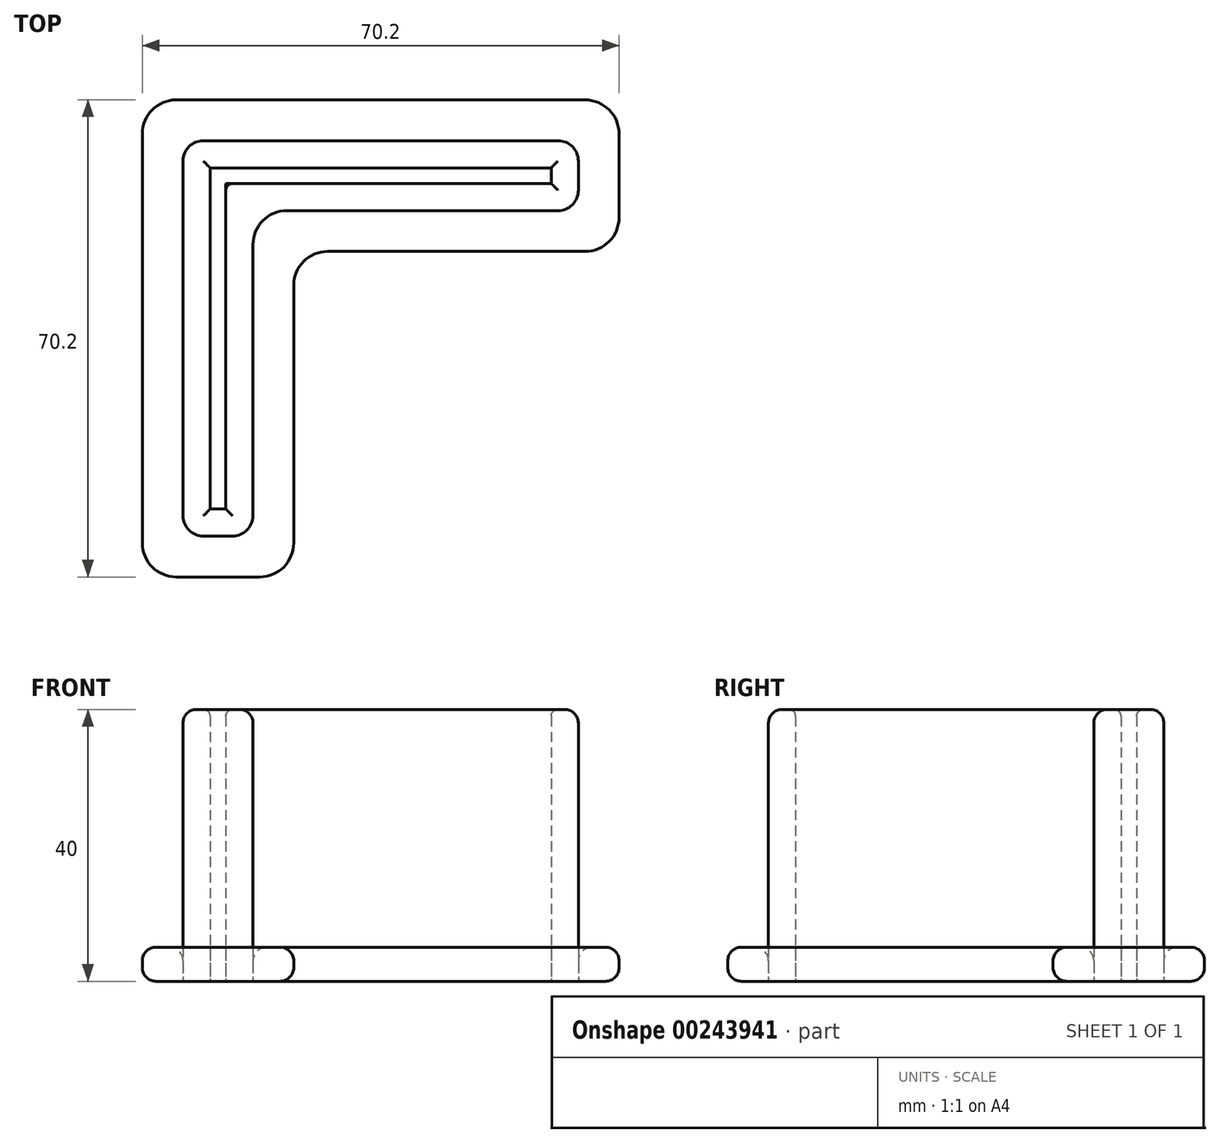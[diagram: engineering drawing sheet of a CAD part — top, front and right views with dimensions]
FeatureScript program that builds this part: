
annotation { "Feature Type Name" : "Feature", "Feature Type Description" : "" }
export const myFeature = defineFeature(function(context is Context, id is Id, definition is map)
    precondition{}
    {
        {
            var Q0;
            Q0=qCreatedBy(makeId("Top.planeOp"),FACE);
            var sketch = newSketch(context, id + "F0", { "sketchPlane" : qUnion([Q0])});
            skLineSegment(sketch, "E0", {"start": v(0, 0) * mm, "end": v(50.2, 0) * mm});
            skLineSegment(sketch, "E1", {"start": v(50.2, 0) * mm, "end": v(50.2, -2.3) * mm});
            skLineSegment(sketch, "E2", {"start": v(50.2, -2.3) * mm, "end": v(2.3, -2.3) * mm});
            skLineSegment(sketch, "E3", {"start": v(0, 0) * mm, "end": v(0, -50.2) * mm});
            skLineSegment(sketch, "E4", {"start": v(0, -50.2) * mm, "end": v(2.3, -50.2) * mm});
            skLineSegment(sketch, "E5", {"start": v(2.3, -50.2) * mm, "end": v(2.3, -2.3) * mm});
            skLineSegment(sketch, "E6.0", {"start": v(-5, 10) * mm, "end": v(55.2, 10) * mm});
            skLineSegment(sketch, "E7.0", {"start": v(60.2, 5) * mm, "end": v(60.2, -7.3) * mm});
            skLineSegment(sketch, "E8.0", {"start": v(55.2, -12.3) * mm, "end": v(17.3, -12.3) * mm});
            skLineSegment(sketch, "E9.0", {"start": v(12.3, -55.2) * mm, "end": v(12.3, -17.3) * mm});
            skLineSegment(sketch, "E10.0", {"start": v(-5, -60.2) * mm, "end": v(7.3, -60.2) * mm});
            skLineSegment(sketch, "E11.0", {"start": v(-10, 5) * mm, "end": v(-10, -55.2) * mm});
            skPoint(sketch, "E12.visualSharp", {"position": v(-10, 10) * mm});
            skArc(sketch, "E12.filletArc", {"start": v(-5, 10) * mm, "mid": v(-8.54, 8.54) * mm, "end": v(-10, 5) * mm});
            skPoint(sketch, "E13.visualSharp", {"position": v(60.2, 10) * mm});
            skArc(sketch, "E13.filletArc", {"start": v(60.2, 5) * mm, "mid": v(58.74, 8.54) * mm, "end": v(55.2, 10) * mm});
            skPoint(sketch, "E14.visualSharp", {"position": v(60.2, -12.3) * mm});
            skArc(sketch, "E14.filletArc", {"start": v(55.2, -12.3) * mm, "mid": v(58.74, -10.84) * mm, "end": v(60.2, -7.3) * mm});
            skPoint(sketch, "E15.visualSharp", {"position": v(12.3, -12.3) * mm});
            skArc(sketch, "E15.filletArc", {"start": v(17.3, -12.3) * mm, "mid": v(13.76, -13.76) * mm, "end": v(12.3, -17.3) * mm});
            skPoint(sketch, "E16.visualSharp", {"position": v(12.3, -60.2) * mm});
            skArc(sketch, "E16.filletArc", {"start": v(7.3, -60.2) * mm, "mid": v(10.84, -58.74) * mm, "end": v(12.3, -55.2) * mm});
            skPoint(sketch, "E17.visualSharp", {"position": v(-10, -60.2) * mm});
            skArc(sketch, "E17.filletArc", {"start": v(-10, -55.2) * mm, "mid": v(-8.54, -58.74) * mm, "end": v(-5, -60.2) * mm});
            skLineSegment(sketch, "E18.0", {"start": v(54.2, 1) * mm, "end": v(54.2, -3.3) * mm});
            skLineSegment(sketch, "E19.0", {"start": v(-1, 4) * mm, "end": v(51.2, 4) * mm});
            skLineSegment(sketch, "E20.0", {"start": v(51.2, -6.3) * mm, "end": v(11.3, -6.3) * mm});
            skLineSegment(sketch, "E21.0", {"start": v(6.3, -51.2) * mm, "end": v(6.3, -11.3) * mm});
            skLineSegment(sketch, "E22.0", {"start": v(-1, -54.2) * mm, "end": v(3.3, -54.2) * mm});
            skLineSegment(sketch, "E23.0", {"start": v(-4, 1) * mm, "end": v(-4, -51.2) * mm});
            skPoint(sketch, "E24.visualSharp", {"position": v(6.3, -6.3) * mm});
            skArc(sketch, "E24.filletArc", {"start": v(11.3, -6.3) * mm, "mid": v(7.76, -7.76) * mm, "end": v(6.3, -11.3) * mm});
            skPoint(sketch, "E25.visualSharp", {"position": v(-4, 4) * mm});
            skArc(sketch, "E25.filletArc", {"start": v(-1, 4) * mm, "mid": v(-3.12, 3.12) * mm, "end": v(-4, 1) * mm});
            skPoint(sketch, "E26.visualSharp", {"position": v(54.2, 4) * mm});
            skArc(sketch, "E26.filletArc", {"start": v(54.2, 1) * mm, "mid": v(53.32, 3.12) * mm, "end": v(51.2, 4) * mm});
            skPoint(sketch, "E27.visualSharp", {"position": v(54.2, -6.3) * mm});
            skArc(sketch, "E27.filletArc", {"start": v(51.2, -6.3) * mm, "mid": v(53.32, -5.42) * mm, "end": v(54.2, -3.3) * mm});
            skPoint(sketch, "E28.visualSharp", {"position": v(6.3, -54.2) * mm});
            skArc(sketch, "E28.filletArc", {"start": v(3.3, -54.2) * mm, "mid": v(5.42, -53.32) * mm, "end": v(6.3, -51.2) * mm});
            skPoint(sketch, "E29.visualSharp", {"position": v(-4, -54.2) * mm});
            skArc(sketch, "E29.filletArc", {"start": v(-4, -51.2) * mm, "mid": v(-3.12, -53.32) * mm, "end": v(-1, -54.2) * mm});
            skSolve(sketch);
        }
        {
            var Q0;
            Q0=makeQuery(id+"F0.imprint","IMPRINT",FACE,{"disambiguationData":[TD([[makeQuery(id+"F0.imprint","IMPRINT",EDGE,{"derivedFrom":sQuery(id+"F0.wireOp",EDGE,"E0")}),-1.0]])]});
            var Q1;
            Q1=makeQuery(id+"F0.imprint","IMPRINT",FACE,{"disambiguationData":[TD([[makeQuery(id+"F0.imprint","IMPRINT",EDGE,{"derivedFrom":sQuery(id+"F0.wireOp",EDGE,"E6.0")}),-1.0]])]});
            extrude(context, id + "F1", {"entities" : qUnion([Q0, Q1]), "depth" : 5 * mm});
        }
        {
            var Q0;
            Q0=makeQuery(id+"F0.imprint","IMPRINT",FACE,{"disambiguationData":[TD([[makeQuery(id+"F0.imprint","IMPRINT",EDGE,{"derivedFrom":sQuery(id+"F0.wireOp",EDGE,"E0")}),1.0]])]});
            extrude(context, id + "F2", {"entities" : qUnion([Q0]), "depth" : 40 * mm});
        }
        {
            var Q0;
            Q0=makeQuery(id+"F1.opExtrude","CAP_EDGE",EDGE,{"disambiguationData":[OSD([sQuery(id+"F0.wireOp",EDGE,"E23.0")])],"isStart":false});
            var Q1;
            Q1=makeQuery(id+"F1.opExtrude","CAP_EDGE",EDGE,{"disambiguationData":[OSD([sQuery(id+"F0.wireOp",EDGE,"E11.0")])],"isStart":false});
            var Q2;
            Q2=makeQuery(id+"F1.opExtrude","CAP_EDGE",EDGE,{"disambiguationData":[OSD([sQuery(id+"F0.wireOp",EDGE,"E11.0")])],"isStart":true});
            var Q3;
            Q3=makeQuery(id+"F2.opExtrude","CAP_EDGE",EDGE,{"disambiguationData":[OSD([sQuery(id+"F0.wireOp",EDGE,"E21.0")])],"isStart":false});
            fillet(context, id + "F3", {"entities" : qUnion([Q0, Q1, Q2, Q3]), "radius" : 2 * mm, "tangentPropagation" : true, "allowEdgeOverflow" : false});
        }
        {
            var Q0;
            Q0=makeQuery(id+"F2.opExtrude","CAP_EDGE",EDGE,{"disambiguationData":[OSD([sQuery(id+"F0.wireOp",EDGE,"E4")])],"isStart":false});
            var Q1;
            Q1=makeQuery(id+"F2.opExtrude","CAP_EDGE",EDGE,{"disambiguationData":[OSD([sQuery(id+"F0.wireOp",EDGE,"E1")])],"isStart":false});
            var Q2;
            Q2=makeQuery(id+"F2.opExtrude","CAP_EDGE",EDGE,{"disambiguationData":[OSD([sQuery(id+"F0.wireOp",EDGE,"E2")])],"isStart":false});
            var Q3;
            Q3=makeQuery(id+"F2.opExtrude","CAP_EDGE",EDGE,{"disambiguationData":[OSD([sQuery(id+"F0.wireOp",EDGE,"E5")])],"isStart":false});
            var Q4;
            Q4=makeQuery(id+"F2.opExtrude","CAP_EDGE",EDGE,{"disambiguationData":[OSD([sQuery(id+"F0.wireOp",EDGE,"E3")])],"isStart":false});
            var Q5;
            Q5=makeQuery(id+"F2.opExtrude","CAP_EDGE",EDGE,{"disambiguationData":[OSD([sQuery(id+"F0.wireOp",EDGE,"E0")])],"isStart":false});
            fillet(context, id + "F4", {"entities" : qUnion([Q0, Q1, Q2, Q3, Q4, Q5]), "radius" : 1 * mm, "tangentPropagation" : true, "allowEdgeOverflow" : false});
        }
        {
            var Q0;
            Q0=makeQuery(id+"F2.opExtrude","SWEPT_EDGE",EDGE,{"disambiguationData":[OSD([sQuery(id+"F0.wireOp",EDGE,"E2"),sQuery(id+"F0.wireOp",EDGE,"E5")])]});
            fillet(context, id + "F5", {"entities" : qUnion([Q0]), "radius" : 1 * mm, "tangentPropagation" : true, "allowEdgeOverflow" : false});
        }
    });
